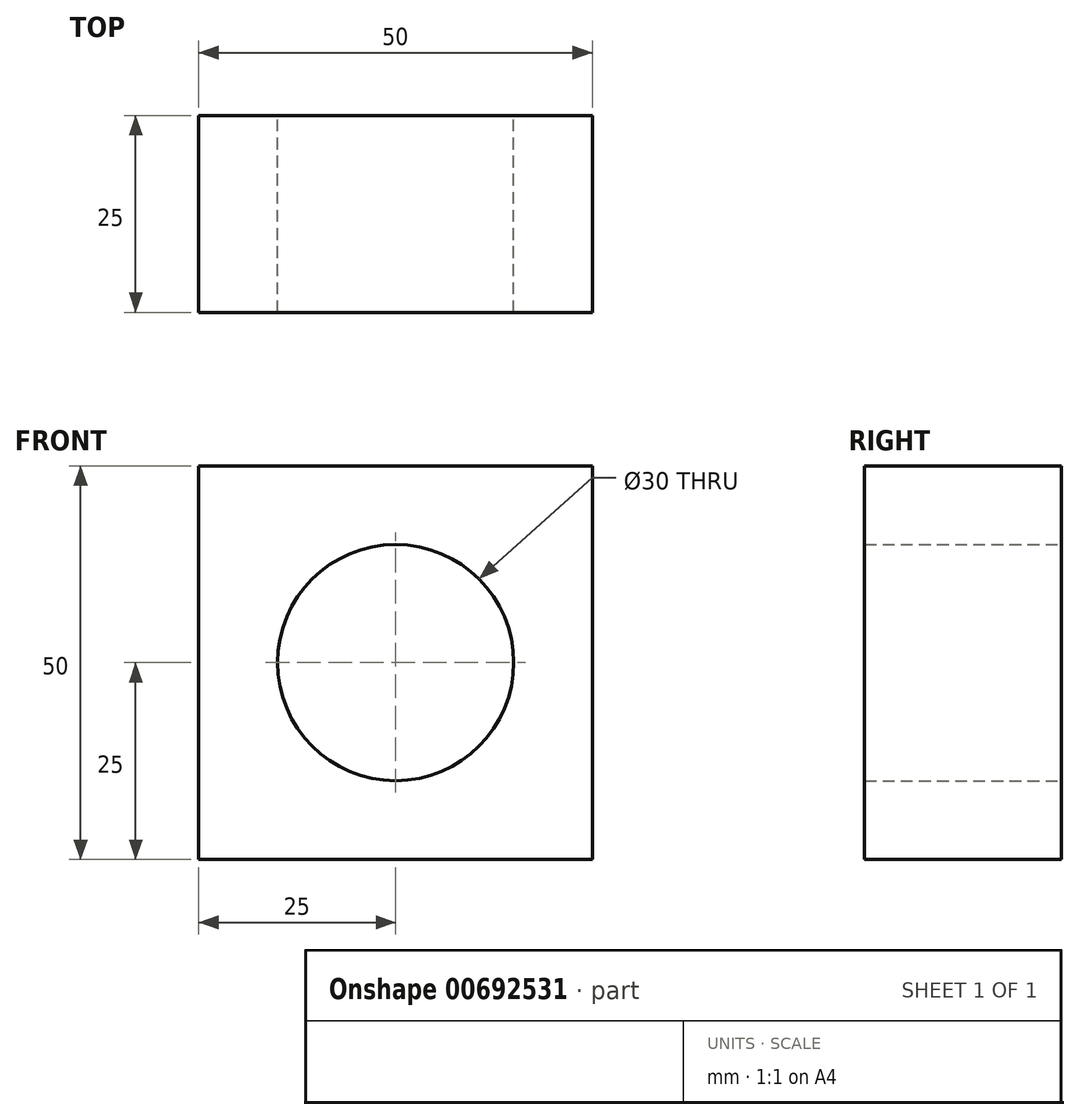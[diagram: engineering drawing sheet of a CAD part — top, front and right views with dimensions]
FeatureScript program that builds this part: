
annotation { "Feature Type Name" : "Feature", "Feature Type Description" : "" }
export const myFeature = defineFeature(function(context is Context, id is Id, definition is map)
    precondition{}
    {
        {
            var Q0;
            Q0=qCreatedBy(makeId("Front.planeOp"),FACE);
            var sketch = newSketch(context, id + "F0", { "sketchPlane" : qUnion([Q0])});
            skLineSegment(sketch, "E0.bottom", {"start": v(25, -25) * mm, "end": v(-25, -25) * mm});
            skLineSegment(sketch, "E0.top", {"start": v(25, 25) * mm, "end": v(-25, 25) * mm});
            skLineSegment(sketch, "E0.left", {"start": v(25, -25) * mm, "end": v(25, 25) * mm});
            skLineSegment(sketch, "E0.right", {"start": v(-25, -25) * mm, "end": v(-25, 25) * mm});
            skPoint(sketch, "E0.middle", {"position": v(0, 0) * mm});
            skCircle(sketch, "E1", {"center": v(0, 0) * mm, "radius": 15 * mm});
            skSolve(sketch);
        }
        {
            var Q0;
            Q0=makeQuery(id+"F0.imprint","IMPRINT",FACE,{"disambiguationData":[TD([[makeQuery(id+"F0.imprint","IMPRINT",EDGE,{"derivedFrom":sQuery(id+"F0.wireOp",EDGE,"E0.bottom")}),-1.0]])]});
            extrude(context, id + "F1", {"entities" : qUnion([Q0]), "depth" : 25 * mm, "offsetDistance" : 25 * mm});
        }
    });
